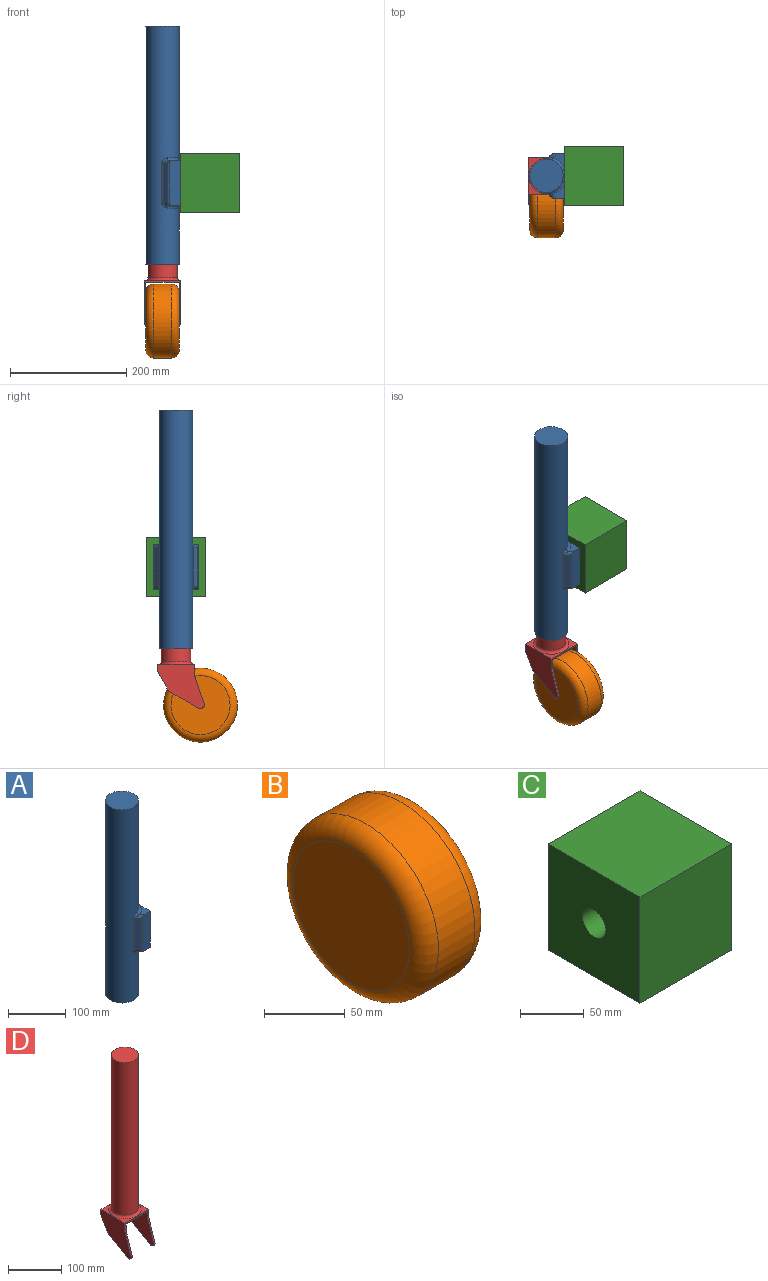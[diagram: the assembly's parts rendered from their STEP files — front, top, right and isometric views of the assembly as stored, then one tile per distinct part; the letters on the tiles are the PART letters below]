
ASSEMBLY  parts=4 mates=3
PART A: 33 faces, bbox 66.9x83.7x409.9 mm
  f0: plane 26.94x21.19mm, normal (0,0,-1), area 262.6mm2, adj f2,f8,f23,f27
  f1: plane 26.94x21.19mm, normal (0,0,1), area 262.6mm2, adj f3,f8,f20,f24
  f2: plane 76.5x20.42mm, normal (0,-1,0), area 1528.5mm2, adj f0,f6,f8,f27,f30,f32
  f3: plane 76.5x20.42mm, normal (0,1,0), area 1528.5mm2, adj f1,f7,f8,f15,f17,f20
  f4: plane 57.15x57.15mm, normal (0,0,-1), area 538.4mm2, adj f9,f12
  f5: cylinder r=3.17mm len=6.35mm, axis (-1,0,0), area 126.7mm2, adj f8,f12
  f6: plane 26.94x21.19mm, normal (0,0,1), area 262.6mm2, adj f2,f8,f29,f32
  f7: plane 26.94x21.19mm, normal (0,0,-1), area 262.6mm2, adj f3,f8,f15,f18
  f8: plane 76.37x76.37mm, normal (1,0,0), area 5774.8mm2, adj f0,f1,f2,f3,f5,f6,f7,f21
  f9: cylinder r=28.57mm len=409.58mm, axis (0,0,-1), area 65575.5mm2, adj f4,f14,f16,f18,f19,f21,f22,f23
  f10: plane 66.04x6.62mm, normal (-0.71,0.71,0), area 618.2mm2, adj f15,f17,f19,f20
  f11: plane 66.04x6.62mm, normal (-0.71,-0.71,0), area 618.2mm2, adj f27,f28,f30,f32
  f12: cylinder r=25.4mm len=406.4mm, axis (0,0,-1), area 64826.8mm2, adj f4,f5,f13
  f13: plane 50.8x50.8mm, normal (0,0,-1), area 2026.8mm2, adj f12
  f14: plane 57.15x57.15mm, normal (0,0,1), area 2565.2mm2, adj f9
  f15: cylinder r=5.08mm len=15.29mm, axis (0.71,0.71,0), area 77.1mm2, adj f3,f7,f10,f16,f17
  f16: bspline ~12.86x10.6mm, area 73mm2, adj f9,f15,f18,f19
  f17: cylinder r=5.08mm len=73.22mm, axis (0,0,-1), area 277.8mm2, adj f3,f10,f15,f20
  f18: torus R=33.65mm, axis (0,0,1), area 221.7mm2, adj f7,f9,f16,f21
  f19: cylinder r=5.08mm len=66.04mm, axis (0,0,-1), area 241.8mm2, adj f9,f10,f16,f22
  f20: cylinder r=5.08mm len=15.29mm, axis (-0.71,-0.71,0), area 77.1mm2, adj f1,f3,f10,f17,f22
  f21: bspline ~25x5.69mm, area 135.2mm2, adj f8,f9,f18,f23
  f22: bspline ~13.92x11.34mm, area 73mm2, adj f9,f19,f20,f24
  f23: torus R=33.65mm, axis (0,0,1), area 221.7mm2, adj f0,f9,f21,f25
  f24: torus R=33.65mm, axis (0,0,1), area 221.7mm2, adj f1,f9,f22,f26
  f25: bspline ~13.92x11.34mm, area 73mm2, adj f9,f23,f27,f28
  f26: bspline ~25x5.69mm, area 135.2mm2, adj f8,f9,f24,f29
  f27: cylinder r=5.08mm len=15.29mm, axis (-0.71,0.71,0), area 77.1mm2, adj f0,f2,f11,f25,f30
  f28: cylinder r=5.08mm len=66.04mm, axis (0,0,-1), area 241.8mm2, adj f9,f11,f25,f31
  f29: torus R=33.65mm, axis (0,0,1), area 221.7mm2, adj f6,f9,f26,f31
  f30: cylinder r=5.08mm len=73.22mm, axis (0,0,1), area 277.8mm2, adj f2,f11,f27,f32
  f31: bspline ~12.86x10.6mm, area 73mm2, adj f9,f28,f29,f32
  f32: cylinder r=5.08mm len=15.29mm, axis (0.71,-0.71,0), area 77.1mm2, adj f2,f6,f11,f30,f31
PART B: 5 faces, bbox 57.2x137.5x137.5 mm
  f0: plane 101.6x101.6mm, normal (1,0,0), area 8107.3mm2, adj f3
  f1: plane 101.6x101.6mm, normal (-1,0,0), area 8107.3mm2, adj f4
  f2: cylinder r=63.5mm len=127mm, axis (-1,0,0), area 12667.7mm2, adj f3,f4
  f3: torus R=50.8mm, axis (-1,0,0), area 7380.9mm2, adj f0,f2
  f4: torus R=50.8mm, axis (-1,0,0), area 7380.9mm2, adj f1,f2
PART C: 8 faces, bbox 101.6x101.6x101.6 mm
  f0: plane 101.6x101.6mm, normal (0,1,0), area 10322.6mm2, adj f1,f3,f4,f5
  f1: plane 101.6x101.6mm, normal (0,0,1), area 10322.6mm2, adj f0,f2,f4,f5
  f2: plane 101.6x101.6mm, normal (0,-1,0), area 10322.6mm2, adj f1,f3,f4,f5
  f3: plane 101.6x101.6mm, normal (0,0,-1), area 10322.6mm2, adj f0,f2,f4,f5
  f4: plane 101.6x101.6mm, normal (1,0,0), area 10322.6mm2, adj f0,f1,f2,f3
  f5: plane 101.6x101.6mm, normal (-1,0,0), area 9815.9mm2, adj f0,f1,f2,f3,f6
  f6: cylinder r=12.7mm len=25.4mm, axis (-1,0,0), area 2026.8mm2, adj f5,f7
  f7: plane 25.4x25.4mm, normal (-1,0,0), area 506.7mm2, adj f6
PART D: 19 faces, bbox 73.8x85.2x431.9 mm
  f0: plane 63.5x19.05mm, normal (0,-1,0), area 302.4mm2, adj f1,f8,f12,f13,f14,f15,f16,f17
  f1: plane 48.88x16.26mm, normal (0,-0.95,0.32), area 163.6mm2, adj f0,f2,f13,f15
  f2: cylinder r=6.35mm len=9.53mm, axis (-1,0,0), area 48.7mm2, adj f1,f3,f13,f15
  f3: plane 51.51x29.74mm, normal (0,0.5,-0.87), area 188.9mm2, adj f2,f4,f13,f15
  f4: plane 33x19.05mm, normal (0,0.87,-0.5), area 121mm2, adj f3,f5,f13,f15
  f5: plane 63.5x12.7mm, normal (0,1,0), area 262.1mm2, adj f4,f11,f12,f13,f14,f15,f16,f17
  f6: cylinder r=25.4mm len=350.52mm, axis (0,0,-1), area 55940.5mm2, adj f7,f18
  f7: plane 50.8x50.8mm, normal (0,0,1), area 2026.8mm2, adj f6
  f8: plane 48.88x16.26mm, normal (0,-0.95,0.32), area 163.6mm2, adj f0,f9,f14,f17
  f9: cylinder r=6.35mm len=9.53mm, axis (-1,0,0), area 48.7mm2, adj f8,f10,f14,f17
  f10: plane 51.51x29.74mm, normal (0,0.5,-0.87), area 188.9mm2, adj f9,f11,f14,f17
  f11: plane 33x19.05mm, normal (0,0.87,-0.5), area 121mm2, adj f5,f10,f14,f17
  f12: plane 63.5x63.5mm, normal (0,0,1), area 1113.6mm2, adj f0,f5,f13,f14,f18
  f13: plane 80.09x76.29mm, normal (1,0,0), area 3663.7mm2, adj f0,f1,f2,f3,f4,f5,f12
  f14: plane 80.09x76.29mm, normal (-1,0,0), area 3663.7mm2, adj f0,f5,f8,f9,f10,f11,f12
  f15: plane 80.09x73.11mm, normal (-1,0,0), area 3462.1mm2, adj f0,f1,f2,f3,f4,f5,f16
  f16: plane 63.5x57.15mm, normal (0,0,-1), area 3629mm2, adj f0,f5,f15,f17
  f17: plane 80.09x73.11mm, normal (1,0,0), area 3462.1mm2, adj f0,f5,f8,f9,f10,f11,f16
  f18: torus R=30.48mm, axis (0,0,1), area 1366mm2, adj f6,f12
PLACE A t=(-323.52,-65.19,-67.76)mm fixed
PLACE B t=(-323.52,-65.19,-95.7)mm
PLACE C rot(axis=(-1,0,0),90deg) t=(-323.64,-204.89,71.94)mm
PLACE D t=(-323.52,-65.19,-95.7)mm
MATE cylindrical B.f2 <-> D.f2  axis (-1,0,0) through (-323.52,-107.17,-165.63)mm
MATE cylindrical D.f6 <-> A.f9  axis (0,0,-1) through (-323.52,-65.19,84.64)mm
MATE cylindrical C.f6 <-> A.f5  axis (-1,0,0) through (-279.19,-65.19,71.94)mm
